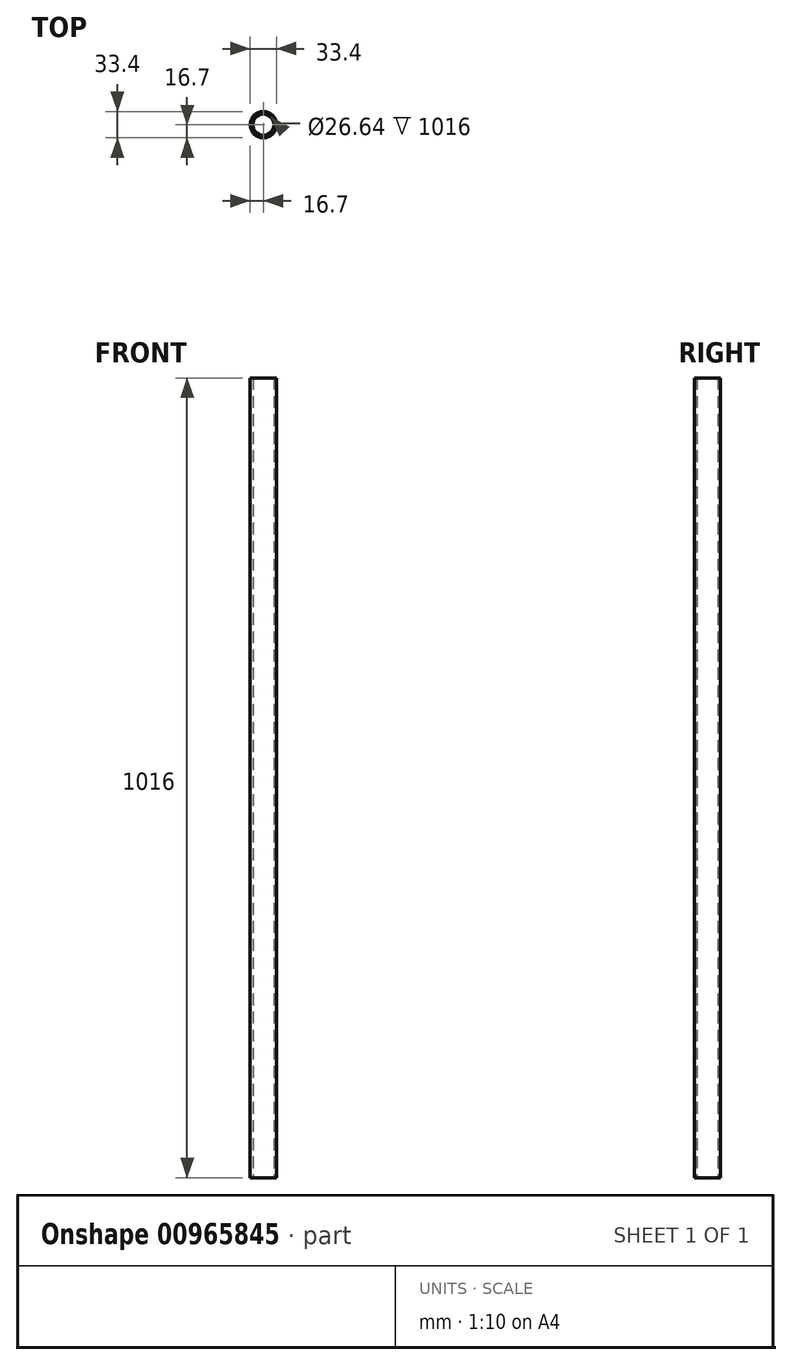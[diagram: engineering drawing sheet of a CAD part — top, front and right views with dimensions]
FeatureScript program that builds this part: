
annotation { "Feature Type Name" : "Feature", "Feature Type Description" : "" }
export const myFeature = defineFeature(function(context is Context, id is Id, definition is map)
    precondition{}
    {
        {
            var Q0;
            Q0=qCreatedBy(makeId("Top.planeOp"),FACE);
            var sketch = newSketch(context, id + "F0", { "sketchPlane" : qUnion([Q0])});
            skCircle(sketch, "E0", {"center": v(0, 0) * mm, "radius": 13.32 * mm});
            skCircle(sketch, "E1", {"center": v(0, 0) * mm, "radius": 16.7 * mm});
            skSolve(sketch);
        }
        {
            var Q0;
            Q0=makeQuery(id+"F0.imprint","IMPRINT",FACE,{"disambiguationData":[TD([[makeQuery(id+"F0.imprint","IMPRINT",EDGE,{"derivedFrom":sQuery(id+"F0.wireOp",EDGE,"E0")}),-1.0]])]});
            extrude(context, id + "F1", {"entities" : qUnion([Q0]), "depth" : 1016 * mm, "offsetDistance" : 25.4 * mm});
        }
    });
